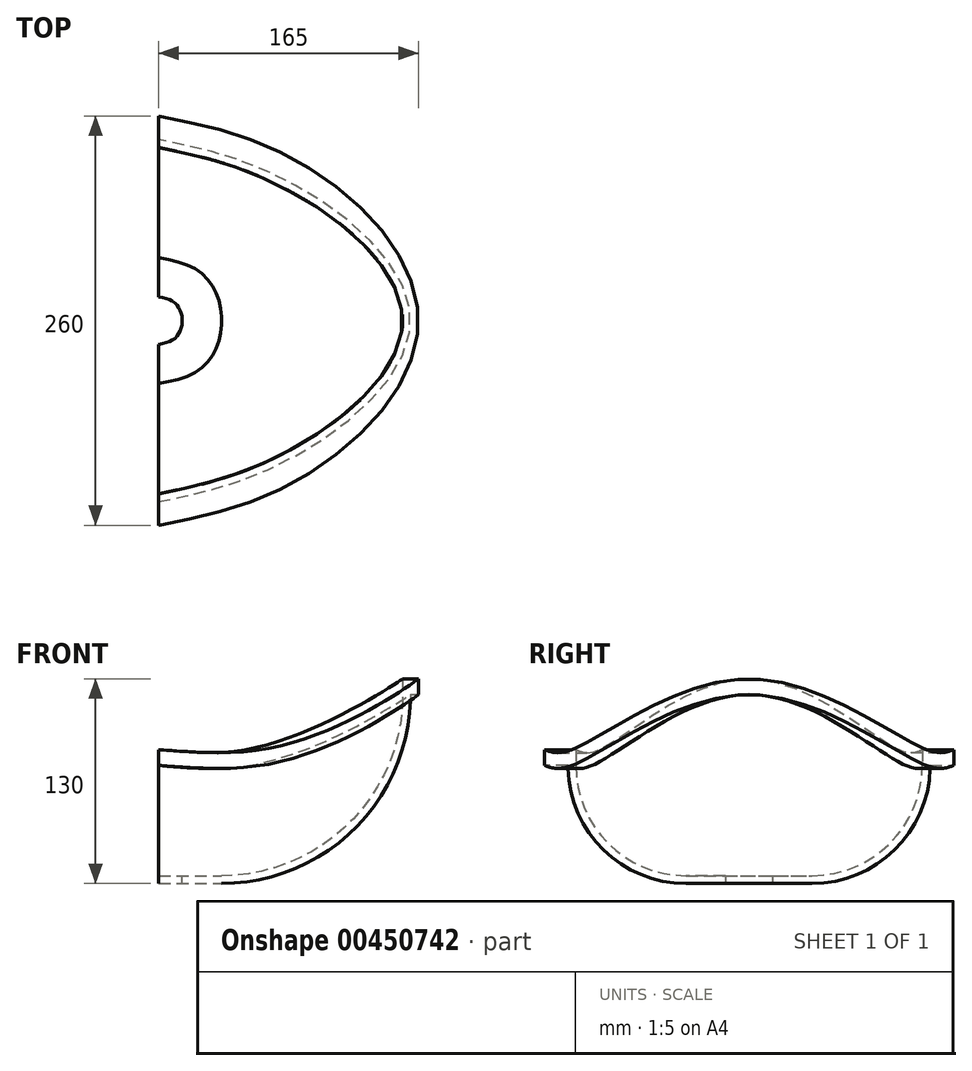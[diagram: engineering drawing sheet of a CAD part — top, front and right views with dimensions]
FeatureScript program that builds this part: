
annotation { "Feature Type Name" : "Feature", "Feature Type Description" : "" }
export const myFeature = defineFeature(function(context is Context, id is Id, definition is map)
    precondition{}
    {
        {
            var Q0;
            Q0=qCreatedBy(makeId("Front.planeOp"),FACE);
            var sketch = newSketch(context, id + "F0", { "sketchPlane" : qUnion([Q0])});
            skLineSegment(sketch, "E0.bottom", {"start": v(15, 5) * mm, "end": v(40, 5) * mm});
            skLineSegment(sketch, "E0.top", {"start": v(15, 0) * mm, "end": v(40, 0) * mm});
            skLineSegment(sketch, "E0.left", {"start": v(15, 5) * mm, "end": v(15, 0) * mm});
            skLineSegment(sketch, "E0.right", {"start": v(40, 5) * mm, "end": v(40, 0) * mm, "construction": true});
            skLineSegment(sketch, "E1.bottom", {"start": v(155, 130) * mm, "end": v(165, 130) * mm});
            skLineSegment(sketch, "E1.top", {"start": v(160, 120) * mm, "end": v(165, 120) * mm});
            skLineSegment(sketch, "E1.left", {"start": v(155, 130) * mm, "end": v(155, 120) * mm});
            skLineSegment(sketch, "E1.right", {"start": v(165, 130) * mm, "end": v(165, 120) * mm});
            skArc(sketch, "E2", {"start": v(40, 0) * mm, "mid": v(124.85, 35.15) * mm, "end": v(160, 120) * mm});
            skArc(sketch, "E3", {"start": v(40, 5) * mm, "mid": v(121.32, 38.68) * mm, "end": v(155, 120) * mm});
            skLineSegment(sketch, "E4", {"start": v(0, 0) * mm, "end": v(0, 50) * mm, "construction": true});
            skSolve(sketch);
        }
        {
            var Q0;
            Q0=sQuery(id+"F0.wireOp",EDGE,"E4");
            cPlane(context, id + "F1", {"entities" : qUnion([Q0]), "cplaneType" : CPlaneType.LINE_ANGLE, "offset" : 25 * mm, "angle" : 30 * degree, "oppositeDirection" : true, "width" : 150 * mm, "height" : 150 * mm});
        }
        {
            var Q0;
            Q0=qCreatedBy(id+"F1.planeOp",FACE);
            var sketch = newSketch(context, id + "F2", { "sketchPlane" : qUnion([Q0])});
            skLineSegment(sketch, "E5.bottom", {"start": v(15, 5) * mm, "end": v(40, 5) * mm});
            skLineSegment(sketch, "E5.top", {"start": v(15, 0) * mm, "end": v(40, 0) * mm});
            skLineSegment(sketch, "E5.left", {"start": v(15, 5) * mm, "end": v(15, 0) * mm});
            skLineSegment(sketch, "E5.right", {"start": v(40, 5) * mm, "end": v(40, 0) * mm, "construction": true});
            skLineSegment(sketch, "E6.bottom", {"start": v(110, 85) * mm, "end": v(130, 85) * mm});
            skLineSegment(sketch, "E6.top", {"start": v(115, 75) * mm, "end": v(130, 75) * mm});
            skLineSegment(sketch, "E6.left", {"start": v(110, 85) * mm, "end": v(110, 75) * mm});
            skLineSegment(sketch, "E6.right", {"start": v(130, 85) * mm, "end": v(130, 75) * mm});
            skArc(sketch, "E7", {"start": v(40, 0) * mm, "mid": v(93.03, 21.97) * mm, "end": v(115, 75) * mm});
            skArc(sketch, "E8", {"start": v(40, 5) * mm, "mid": v(89.5, 25.5) * mm, "end": v(110, 75) * mm});
            skLineSegment(sketch, "E9", {"start": v(0, 0) * mm, "end": v(0, 50) * mm, "construction": true});
            skSolve(sketch);
        }
        {
            var Q0;
            Q0=sQuery(id+"F2.wireOp",EDGE,"E9");
            cPlane(context, id + "F3", {"entities" : qUnion([Q0]), "cplaneType" : CPlaneType.LINE_ANGLE, "offset" : 25 * mm, "angle" : 150 * degree, "oppositeDirection" : true, "width" : 150 * mm, "height" : 150 * mm});
        }
        {
            var Q0;
            Q0=qCreatedBy(id+"F3.planeOp",FACE);
            var sketch = newSketch(context, id + "F4", { "sketchPlane" : qUnion([Q0])});
            skLineSegment(sketch, "E10.bottom", {"start": v(15, 5) * mm, "end": v(40, 5) * mm});
            skLineSegment(sketch, "E10.top", {"start": v(15, 0) * mm, "end": v(40, 0) * mm});
            skLineSegment(sketch, "E10.left", {"start": v(15, 5) * mm, "end": v(15, 0) * mm});
            skLineSegment(sketch, "E10.right", {"start": v(40, 5) * mm, "end": v(40, 0) * mm, "construction": true});
            skLineSegment(sketch, "E11.bottom", {"start": v(110, 85) * mm, "end": v(130, 85) * mm});
            skLineSegment(sketch, "E11.top", {"start": v(115, 75) * mm, "end": v(130, 75) * mm});
            skLineSegment(sketch, "E11.left", {"start": v(110, 85) * mm, "end": v(110, 75) * mm});
            skLineSegment(sketch, "E11.right", {"start": v(130, 85) * mm, "end": v(130, 75) * mm});
            skArc(sketch, "E12", {"start": v(40, 0) * mm, "mid": v(93.03, 21.97) * mm, "end": v(115, 75) * mm});
            skArc(sketch, "E13", {"start": v(40, 5) * mm, "mid": v(89.5, 25.5) * mm, "end": v(110, 75) * mm});
            skLineSegment(sketch, "E14", {"start": v(0, 0) * mm, "end": v(0, 50) * mm, "construction": true});
            skSolve(sketch);
        }
        {
            var Q0;
            Q0=qCreatedBy(makeId("Right.planeOp"),FACE);
            var sketch = newSketch(context, id + "F5", { "sketchPlane" : qUnion([Q0])});
            skLineSegment(sketch, "E15.bottom", {"start": v(15, 5) * mm, "end": v(40, 5) * mm});
            skLineSegment(sketch, "E15.top", {"start": v(15, 0) * mm, "end": v(40, 0) * mm});
            skLineSegment(sketch, "E15.left", {"start": v(15, 5) * mm, "end": v(15, 0) * mm});
            skLineSegment(sketch, "E15.right", {"start": v(40, 5) * mm, "end": v(40, 0) * mm, "construction": true});
            skLineSegment(sketch, "E16.bottom", {"start": v(110, 85) * mm, "end": v(130, 85) * mm});
            skLineSegment(sketch, "E16.top", {"start": v(115, 75) * mm, "end": v(130, 75) * mm});
            skLineSegment(sketch, "E16.left", {"start": v(110, 85) * mm, "end": v(110, 75) * mm});
            skLineSegment(sketch, "E16.right", {"start": v(130, 85) * mm, "end": v(130, 75) * mm});
            skArc(sketch, "E17", {"start": v(40, 0) * mm, "mid": v(93.03, 21.97) * mm, "end": v(115, 75) * mm});
            skArc(sketch, "E18", {"start": v(40, 5) * mm, "mid": v(89.5, 25.5) * mm, "end": v(110, 75) * mm});
            skLineSegment(sketch, "E19", {"start": v(0, 0) * mm, "end": v(0, 50) * mm, "construction": true});
            skSolve(sketch);
        }
        {
            var Q0;
            Q0=sQuery(id+"F5.wireOp",EDGE,"E19");
            cPlane(context, id + "F6", {"entities" : qUnion([Q0]), "cplaneType" : CPlaneType.LINE_ANGLE, "offset" : 25 * mm, "angle" : 180 * degree, "width" : 150 * mm, "height" : 150 * mm});
        }
        {
            var Q0;
            Q0=qCreatedBy(id+"F6.planeOp",FACE);
            var sketch = newSketch(context, id + "F7", { "sketchPlane" : qUnion([Q0])});
            skLineSegment(sketch, "E20.bottom", {"start": v(15, 5) * mm, "end": v(40, 5) * mm});
            skLineSegment(sketch, "E20.top", {"start": v(15, 0) * mm, "end": v(40, 0) * mm});
            skLineSegment(sketch, "E20.left", {"start": v(15, 5) * mm, "end": v(15, 0) * mm});
            skLineSegment(sketch, "E20.right", {"start": v(40, 5) * mm, "end": v(40, 0) * mm, "construction": true});
            skLineSegment(sketch, "E21.bottom", {"start": v(110, 85) * mm, "end": v(130, 85) * mm});
            skLineSegment(sketch, "E21.top", {"start": v(115, 75) * mm, "end": v(130, 75) * mm});
            skLineSegment(sketch, "E21.left", {"start": v(110, 85) * mm, "end": v(110, 75) * mm});
            skLineSegment(sketch, "E21.right", {"start": v(130, 85) * mm, "end": v(130, 75) * mm});
            skArc(sketch, "E22", {"start": v(40, 0) * mm, "mid": v(93.03, 21.97) * mm, "end": v(115, 75) * mm});
            skArc(sketch, "E23", {"start": v(40, 5) * mm, "mid": v(89.5, 25.5) * mm, "end": v(110, 75) * mm});
            skLineSegment(sketch, "E24", {"start": v(0, 0) * mm, "end": v(0, 50) * mm, "construction": true});
            skSolve(sketch);
        }
        {
            var Q0;
            Q0=makeQuery(id+"F7.imprint","IMPRINT",FACE,{"disambiguationData":[TD([[makeQuery(id+"F7.imprint","IMPRINT",EDGE,{"derivedFrom":sQuery(id+"F7.wireOp",EDGE,"E20.bottom")}),-1.0]])]});
            var Q1;
            Q1=makeQuery(id+"F4.imprint","IMPRINT",FACE,{"disambiguationData":[TD([[makeQuery(id+"F4.imprint","IMPRINT",EDGE,{"derivedFrom":sQuery(id+"F4.wireOp",EDGE,"E10.bottom")}),-1.0]])]});
            var Q2;
            Q2=makeQuery(id+"F0.imprint","IMPRINT",FACE,{"disambiguationData":[TD([[makeQuery(id+"F0.imprint","IMPRINT",EDGE,{"derivedFrom":sQuery(id+"F0.wireOp",EDGE,"E0.bottom")}),-1.0]])]});
            var Q3;
            Q3=makeQuery(id+"F2.imprint","IMPRINT",FACE,{"disambiguationData":[TD([[makeQuery(id+"F2.imprint","IMPRINT",EDGE,{"derivedFrom":sQuery(id+"F2.wireOp",EDGE,"E5.bottom")}),-1.0]])]});
            var Q4;
            Q4=makeQuery(id+"F5.imprint","IMPRINT",FACE,{"disambiguationData":[TD([[makeQuery(id+"F5.imprint","IMPRINT",EDGE,{"derivedFrom":sQuery(id+"F5.wireOp",EDGE,"E15.bottom")}),-1.0]])]});
            loft(context, id + "F8", {"sheetProfilesArray" : [{ "sheetProfileEntities" : qUnion([Q0]) }, { "sheetProfileEntities" : qUnion([Q1]) }, { "sheetProfileEntities" : qUnion([Q2]) }, { "sheetProfileEntities" : qUnion([Q3]) }, { "sheetProfileEntities" : qUnion([Q4]) }]});
        }
    });
